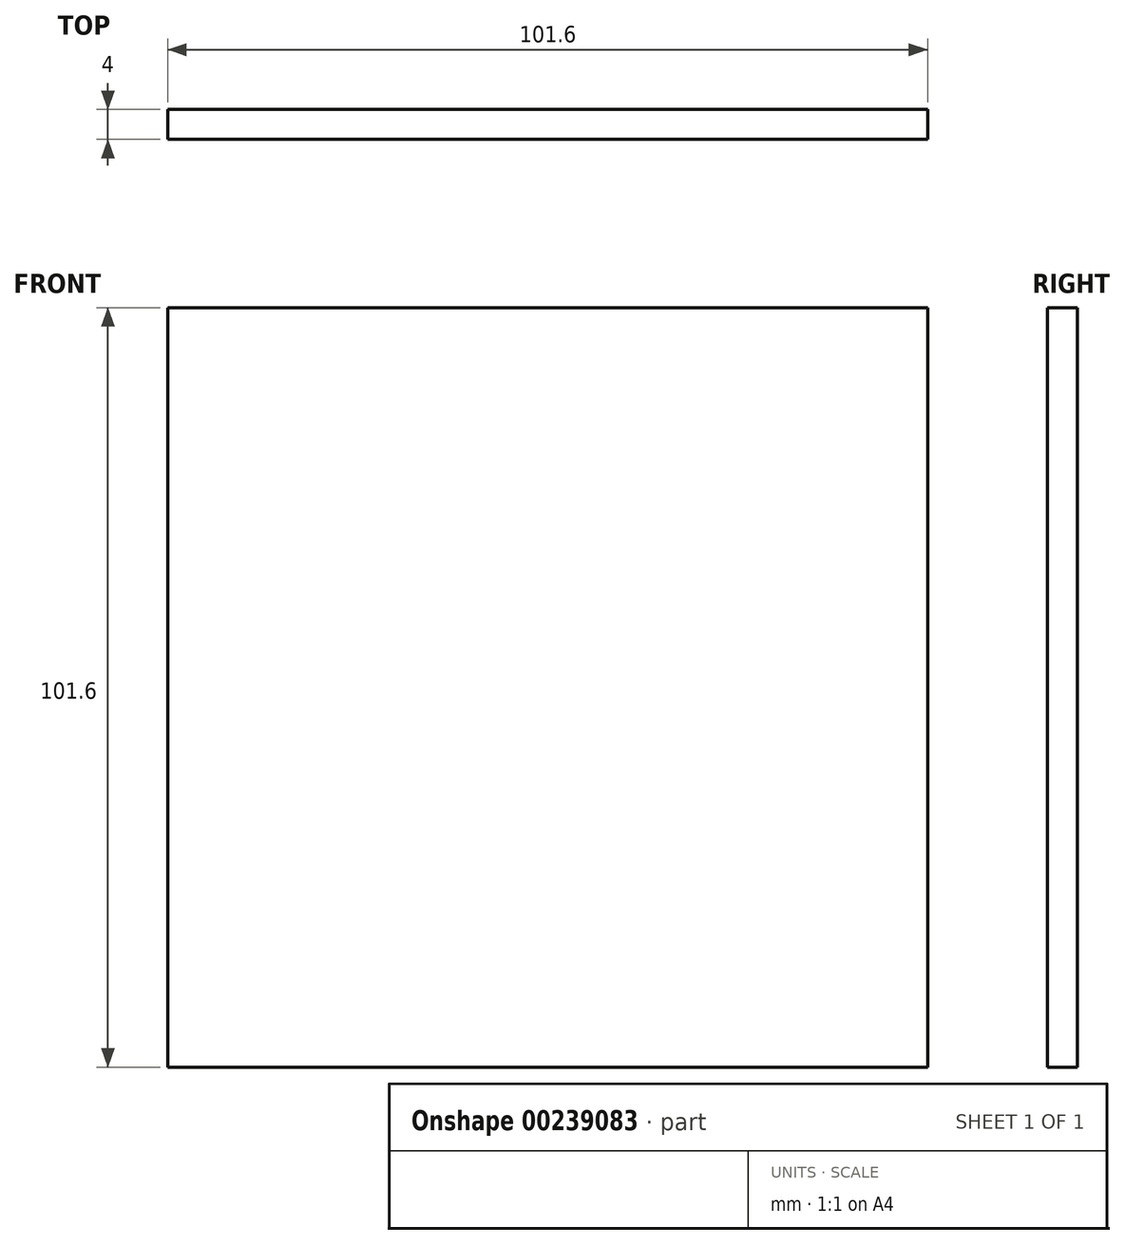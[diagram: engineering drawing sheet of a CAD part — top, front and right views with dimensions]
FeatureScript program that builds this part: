
annotation { "Feature Type Name" : "Feature", "Feature Type Description" : "" }
export const myFeature = defineFeature(function(context is Context, id is Id, definition is map)
    precondition{}
    {
        {
            assignVariable(context, id + "F0", {"name" : "v", "anyValue" : 4});
        }
        {
            var Q0;
            Q0=qCreatedBy(makeId("Front.planeOp"),FACE);
            var sketch = newSketch(context, id + "F1", { "sketchPlane" : qUnion([Q0])});
            skLineSegment(sketch, "E0.bottom", {"start": v(-50.8, 50.8) * mm, "end": v(50.8, 50.8) * mm});
            skLineSegment(sketch, "E0.top", {"start": v(-50.8, -50.8) * mm, "end": v(50.8, -50.8) * mm});
            skLineSegment(sketch, "E0.left", {"start": v(-50.8, 50.8) * mm, "end": v(-50.8, -50.8) * mm});
            skLineSegment(sketch, "E0.right", {"start": v(50.8, 50.8) * mm, "end": v(50.8, -50.8) * mm});
            skPoint(sketch, "E0.middle", {"position": v(0, 0) * mm});
            skSolve(sketch);
        }
        {
            var Q0;
            Q0 = qSketchRegion(id + "F1", true);
            extrude(context, id + "F2", {"entities" : qUnion([Q0]), "endBound" : BoundingType.SYMMETRIC, "depth" : (getVariable(context, 'v')) * mm});
        }
        {
            var Q0;
            Q0=makeQuery(id+"F2.opExtrude","CAP_FACE",FACE,{"disambiguationData":[OSD([sQuery(id+"F1.wireOp",EDGE,"E0.bottom"),sQuery(id+"F1.wireOp",EDGE,"E0.top"),sQuery(id+"F1.wireOp",EDGE,"E0.left"),sQuery(id+"F1.wireOp",EDGE,"E0.right")])],"isStart":false});
            var sketch = newSketch(context, id + "F3", { "sketchPlane" : qUnion([Q0])});
            skLineSegment(sketch, "E1.bottom", {"start": v(-19.05, 19.05) * mm, "end": v(19.05, 19.05) * mm});
            skLineSegment(sketch, "E1.top", {"start": v(-19.05, -19.05) * mm, "end": v(19.05, -19.05) * mm});
            skLineSegment(sketch, "E1.left", {"start": v(-19.05, 19.05) * mm, "end": v(-19.05, -19.05) * mm});
            skLineSegment(sketch, "E1.right", {"start": v(19.05, 19.05) * mm, "end": v(19.05, -19.05) * mm});
            skPoint(sketch, "E1.middle", {"position": v(0, 0) * mm});
            skSolve(sketch);
        }
        {
            var Q0;
            Q0=makeQuery(id+"F3.imprint","IMPRINT",FACE,{"disambiguationData":[TD([[makeQuery(id+"F3.imprint","IMPRINT",EDGE,{"derivedFrom":sQuery(id+"F3.wireOp",EDGE,"E1.bottom")}),-1.0]])]});
            extrude(context, id + "F4", {"entities" : qUnion([Q0]), "operationType" : NewBodyOperationType.ADD, "depth" : 25.4 * mm});
        }
        {
            var Q0;
            Q0=makeQuery(id+"F4.opExtrude","CAP_FACE",FACE,{"disambiguationData":[OSD([sQuery(id+"F3.wireOp",EDGE,"E1.bottom"),sQuery(id+"F3.wireOp",EDGE,"E1.top"),sQuery(id+"F3.wireOp",EDGE,"E1.left"),sQuery(id+"F3.wireOp",EDGE,"E1.right")])],"isStart":false});
            extrude(context, id + "F5", {"entities" : qUnion([Q0]), "operationType" : NewBodyOperationType.REMOVE, "oppositeDirection" : true, "depth" : 25.4 * mm});
        }
    });
